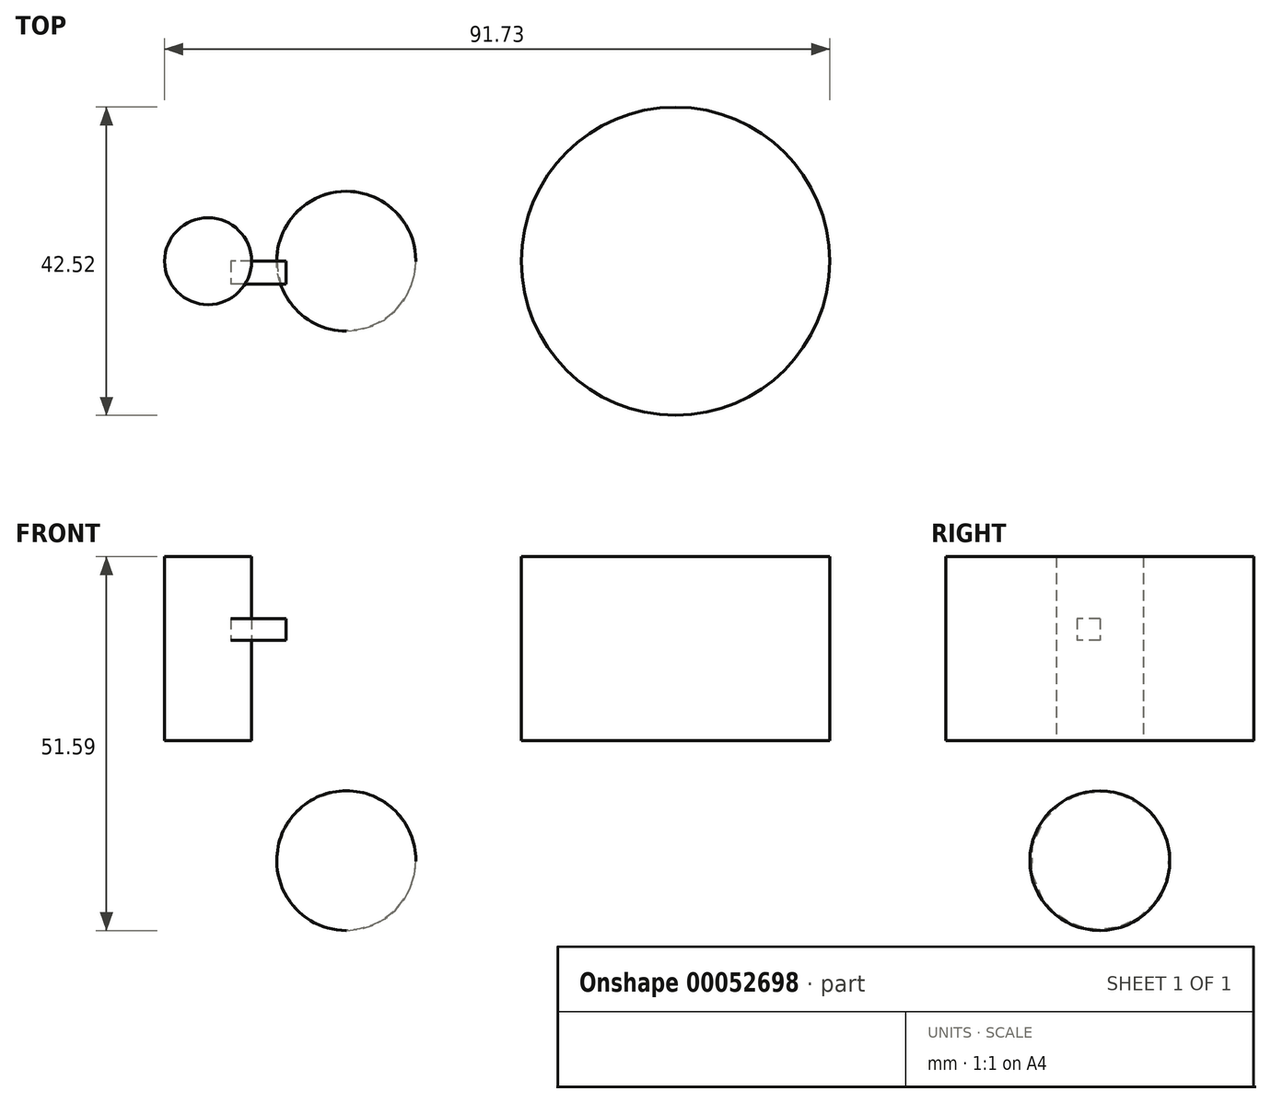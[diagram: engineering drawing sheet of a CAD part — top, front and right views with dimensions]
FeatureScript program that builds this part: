
annotation { "Feature Type Name" : "Feature", "Feature Type Description" : "" }
export const myFeature = defineFeature(function(context is Context, id is Id, definition is map)
    precondition{}
    {
        {
            var Q0;
            Q0=qCreatedBy(makeId("Top.planeOp"),FACE);
            var sketch = newSketch(context, id + "F0", { "sketchPlane" : qUnion([Q0])});
            skCircle(sketch, "E0", {"center": v(0, 0) * mm, "radius": 21.26 * mm});
            skSolve(sketch);
        }
        {
            var Q0;
            Q0=makeQuery(id+"F0.imprint","IMPRINT",FACE,{"disambiguationData":[TD([[makeQuery(id+"F0.imprint","IMPRINT",EDGE,{"derivedFrom":sQuery(id+"F0.wireOp",EDGE,"E0")}),1.0]])]});
            extrude(context, id + "F1", {"entities" : qUnion([Q0]), "depth" : 25.4 * mm});
        }
        {
            var Q0;
            Q0=qCreatedBy(makeId("Top.planeOp"),FACE);
            var sketch = newSketch(context, id + "F2", { "sketchPlane" : qUnion([Q0])});
            skCircle(sketch, "E1", {"center": v(-64.47, 0) * mm, "radius": 6 * mm});
            skSolve(sketch);
        }
        {
            var Q0;
            Q0=makeQuery(id+"F2.imprint","IMPRINT",FACE,{"disambiguationData":[TD([[makeQuery(id+"F2.imprint","IMPRINT",EDGE,{"derivedFrom":sQuery(id+"F2.wireOp",EDGE,"E1")}),1.0]])]});
            extrude(context, id + "F3", {"entities" : qUnion([Q0]), "depth" : 25.4 * mm});
        }
        {
            var Q0;
            Q0=qCreatedBy(makeId("Right.planeOp"),FACE);
            var sketch = newSketch(context, id + "F4", { "sketchPlane" : qUnion([Q0])});
            skLineSegment(sketch, "E2.bottom", {"start": v(0, 41.47) * mm, "end": v(-3.13, 41.47) * mm});
            skLineSegment(sketch, "E2.top", {"start": v(0, 38.44) * mm, "end": v(-3.13, 38.44) * mm});
            skLineSegment(sketch, "E2.left", {"start": v(0, 41.47) * mm, "end": v(0, 38.44) * mm});
            skLineSegment(sketch, "E2.right", {"start": v(-3.13, 41.47) * mm, "end": v(-3.13, 38.44) * mm});
            skSolve(sketch);
        }
        {
            var Q0;
            Q0=makeQuery(id+"F4.imprint","IMPRINT",FACE,{"disambiguationData":[TD([[makeQuery(id+"F4.imprint","IMPRINT",EDGE,{"derivedFrom":sQuery(id+"F4.wireOp",EDGE,"E2.bottom")}),1.0]])]});
            extrude(context, id + "F5", {"entities" : qUnion([Q0]), "depth" : 7.62 * mm});
        }
        {
            var Q0;
            Q0=makeQuery(id+"F5.opExtrude","SWEPT_BODY",BODY,{"disambiguationData":[OSD([sQuery(id+"F4.wireOp",EDGE,"E2.bottom"),sQuery(id+"F4.wireOp",EDGE,"E2.top"),sQuery(id+"F4.wireOp",EDGE,"E2.left"),sQuery(id+"F4.wireOp",EDGE,"E2.right")])]});
            transform(context, id + "F6", {"entities" : qUnion([Q0]), "transformType" : TransformType.TRANSLATION_3D, "dx" : -61.34 * mm, "dy" : 0 * mm, "dz" : -24.62 * mm, "makeCopy" : false});
        }
        {
            var Q0;
            Q0=qCreatedBy(makeId("Top.planeOp"),FACE);
            var sketch = newSketch(context, id + "F7", { "sketchPlane" : qUnion([Q0])});
            skArc(sketch, "E3", {"start": v(-73.75, 0) * mm, "mid": v(-64.17, -9.64) * mm, "end": v(-54.58, 0) * mm});
            skLineSegment(sketch, "E4", {"start": v(-73.75, 0) * mm, "end": v(-54.58, 0) * mm});
            skSolve(sketch);
        }
        {
            var Q0;
            Q0=makeQuery(id+"F7.imprint","IMPRINT",FACE,{"disambiguationData":[TD([[makeQuery(id+"F7.imprint","IMPRINT",EDGE,{"derivedFrom":sQuery(id+"F7.wireOp",EDGE,"E3")}),1.0]])]});
            var Q1;
            Q1=sQuery(id+"F7.wireOp",EDGE,"E4");
            revolve(context, id + "F8", {"entities" : qUnion([Q0]), "axis" : qUnion([Q1]), "revolveType" : RevolveType.FULL});
        }
        {
            var Q0;
            Q0=makeQuery(id+"F8.opRevolve","SWEPT_BODY",BODY,{"disambiguationData":[OSD([sQuery(id+"F7.wireOp",EDGE,"E3"),sQuery(id+"F7.wireOp",EDGE,"E4")])]});
            transform(context, id + "F9", {"entities" : qUnion([Q0]), "transformType" : TransformType.TRANSLATION_3D, "dx" : 18.77 * mm, "dy" : 0 * mm, "dz" : -16.55 * mm, "makeCopy" : false});
        }
    });
